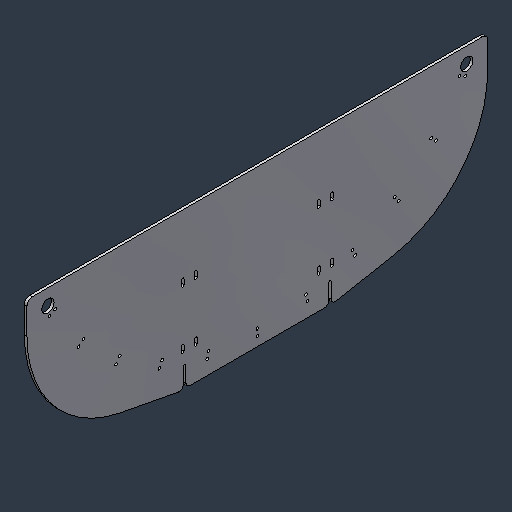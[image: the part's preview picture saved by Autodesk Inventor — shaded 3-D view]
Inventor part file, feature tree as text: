
AUTODESK INVENTOR PART (.ipt)
format: ipt  version: 2024.3 (Build 283343000, 343)  size: 151,040 bytes
history: native  units: mm (DEFAULTED — no unit token found)
features: fillet x1
ambient origin geometry x8: Origin, YZ Plane, XZ Plane, XY Plane, X Axis, Y Axis, Z Axis, Center Point
bodies: Solid1 (feature_tree)
feature tree (1):
  fillet  "Fillet4"  [1 undecoded]
note: 1 required parameter value undecoded (feature->parameter linkage not recoverable at this tier; creation-order binding heuristic only, values carry confidence <= 0.55)
